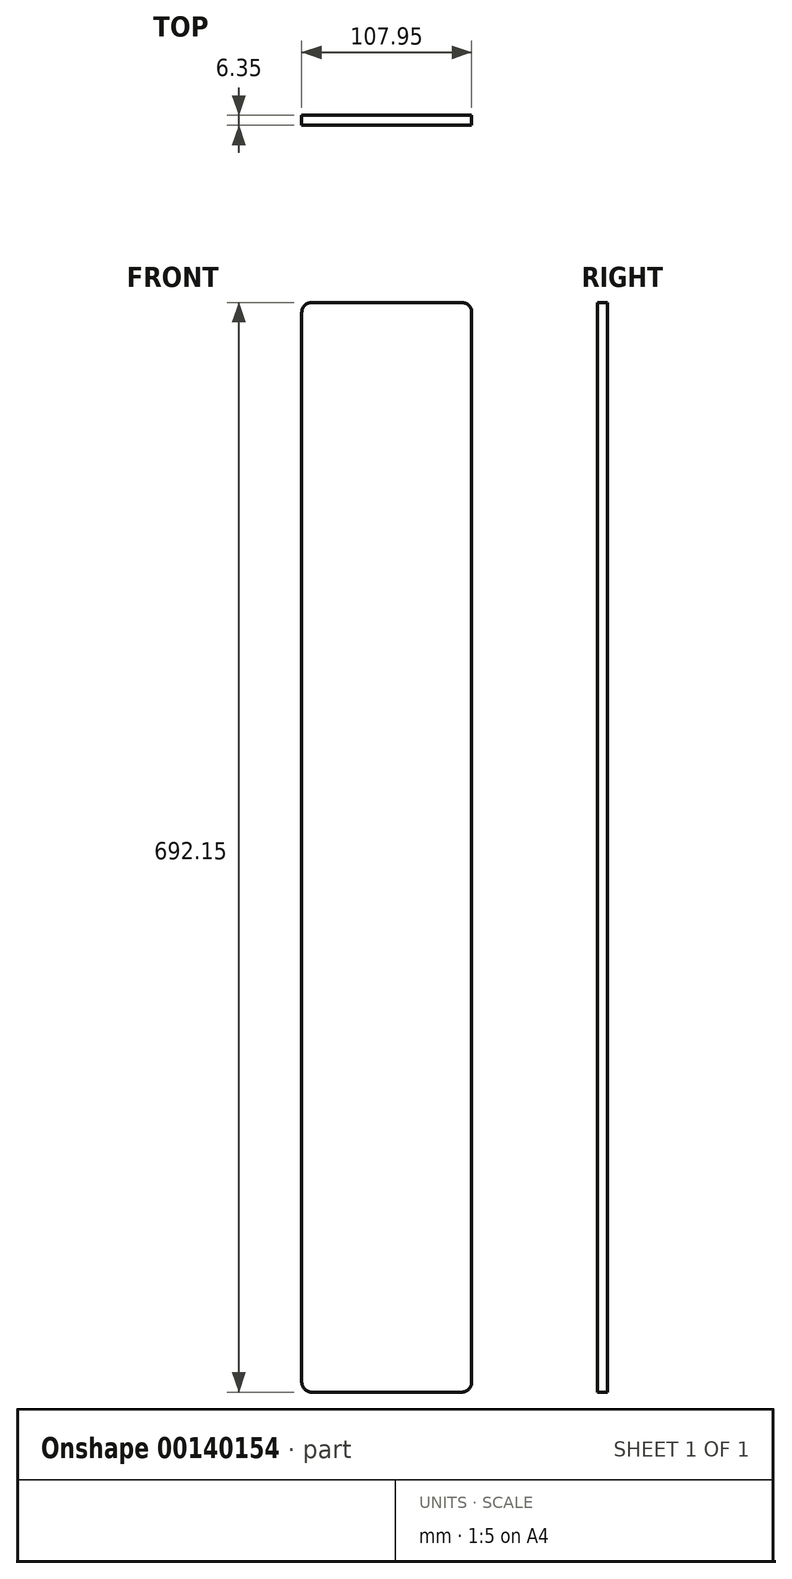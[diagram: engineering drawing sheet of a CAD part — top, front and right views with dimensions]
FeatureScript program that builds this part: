
annotation { "Feature Type Name" : "Feature", "Feature Type Description" : "" }
export const myFeature = defineFeature(function(context is Context, id is Id, definition is map)
    precondition{}
    {
        {
            var Q0;
            Q0=qCreatedBy(makeId("Front.planeOp"),FACE);
            var sketch = newSketch(context, id + "F0", { "sketchPlane" : qUnion([Q0])});
            skLineSegment(sketch, "E0", {"start": v(-628.65, 717.55) * mm, "end": v(-628.65, 38.1) * mm});
            skLineSegment(sketch, "E1.trimOffspring", {"start": v(-635, 723.9) * mm, "end": v(-730.25, 723.9) * mm});
            skPoint(sketch, "E2.visualSharp", {"position": v(-628.65, 723.9) * mm});
            skArc(sketch, "E2.filletArc", {"start": v(-628.65, 717.55) * mm, "mid": v(-630.5, 722.04) * mm, "end": v(-635, 723.9) * mm});
            skLineSegment(sketch, "E3", {"start": v(-730.25, 31.75) * mm, "end": v(-635, 31.75) * mm});
            skPoint(sketch, "E4.visualSharp", {"position": v(-628.65, 31.75) * mm});
            skArc(sketch, "E4.filletArc", {"start": v(-635, 31.75) * mm, "mid": v(-630.5, 33.6) * mm, "end": v(-628.65, 38.1) * mm});
            skLineSegment(sketch, "E5", {"start": v(-736.6, 38.1) * mm, "end": v(-736.6, 717.55) * mm});
            skPoint(sketch, "E6.visualSharp", {"position": v(-736.6, 31.75) * mm});
            skArc(sketch, "E6.filletArc", {"start": v(-736.6, 38.1) * mm, "mid": v(-734.74, 33.6) * mm, "end": v(-730.25, 31.75) * mm});
            skPoint(sketch, "E7.visualSharp", {"position": v(-736.6, 723.9) * mm});
            skArc(sketch, "E7.filletArc", {"start": v(-730.25, 723.9) * mm, "mid": v(-734.74, 722.04) * mm, "end": v(-736.6, 717.55) * mm});
            skSolve(sketch);
        }
        {
            var Q0;
            Q0=makeQuery(id+"F0.imprint","IMPRINT",FACE,{"disambiguationData":[TD([[makeQuery(id+"F0.imprint","IMPRINT",EDGE,{"derivedFrom":sQuery(id+"F0.wireOp",EDGE,"E0")}),-1.0]])]});
            extrude(context, id + "F1", {"entities" : qUnion([Q0]), "depth" : 6.35 * mm});
        }
    });
